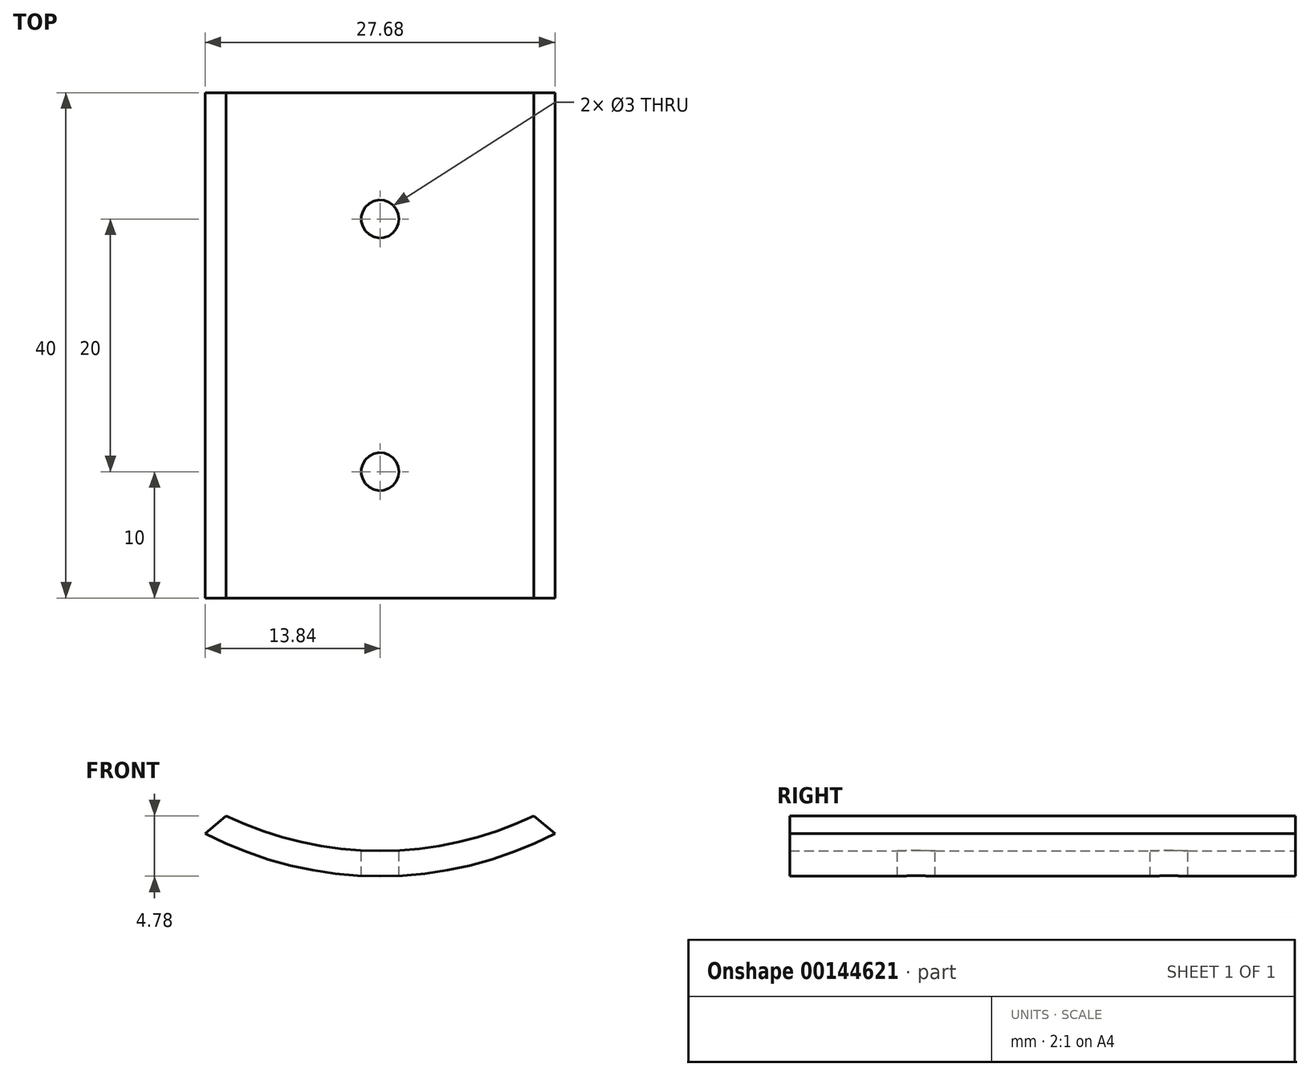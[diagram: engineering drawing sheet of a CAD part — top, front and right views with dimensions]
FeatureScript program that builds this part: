
annotation { "Feature Type Name" : "Feature", "Feature Type Description" : "" }
export const myFeature = defineFeature(function(context is Context, id is Id, definition is map)
    precondition{}
    {
        {
            var Q0;
            Q0=qCreatedBy(makeId("Front.planeOp"),FACE);
            var sketch = newSketch(context, id + "F0", { "sketchPlane" : qUnion([Q0])});
            skArc(sketch, "E0", {"start": v(-13.84, -26.62) * mm, "mid": v(0, -30) * mm, "end": v(13.84, -26.62) * mm});
            skLineSegment(sketch, "E1", {"start": v(0, -30) * mm, "end": v(0, -15) * mm, "construction": true});
            skArc(sketch, "E2.0", {"start": v(-12.17, -25.22) * mm, "mid": v(0, -28) * mm, "end": v(12.17, -25.22) * mm});
            skLineSegment(sketch, "E3", {"start": v(12.17, -25.22) * mm, "end": v(13.84, -26.62) * mm});
            skLineSegment(sketch, "E4", {"start": v(0, -15) * mm, "end": v(12.17, -25.22) * mm, "construction": true});
            skLineSegment(sketch, "E5", {"start": v(0, -15) * mm, "end": v(-12.17, -25.22) * mm, "construction": true});
            skLineSegment(sketch, "E6", {"start": v(-13.84, -26.62) * mm, "end": v(-12.17, -25.22) * mm});
            skSolve(sketch);
        }
        {
            var Q0;
            Q0 = qSketchRegion(id + "F0", true);
            extrude(context, id + "F1", {"entities" : qUnion([Q0]), "endBound" : BoundingType.SYMMETRIC, "depth" : 40 * mm});
        }
        {
            var Q0;
            Q0=qCreatedBy(makeId("Top.planeOp"),FACE);
            var sketch = newSketch(context, id + "F2", { "sketchPlane" : qUnion([Q0])});
            skCircle(sketch, "E7", {"center": v(0, -10) * mm, "radius": 1.5 * mm});
            skCircle(sketch, "E8", {"center": v(0, 10) * mm, "radius": 1.5 * mm});
            skSolve(sketch);
        }
        {
            var Q0;
            Q0 = qSketchRegion(id + "F2", true);
            extrude(context, id + "F3", {"entities" : qUnion([Q0]), "operationType" : NewBodyOperationType.REMOVE, "oppositeDirection" : true, "depth" : 54.84 * mm});
        }
    });
